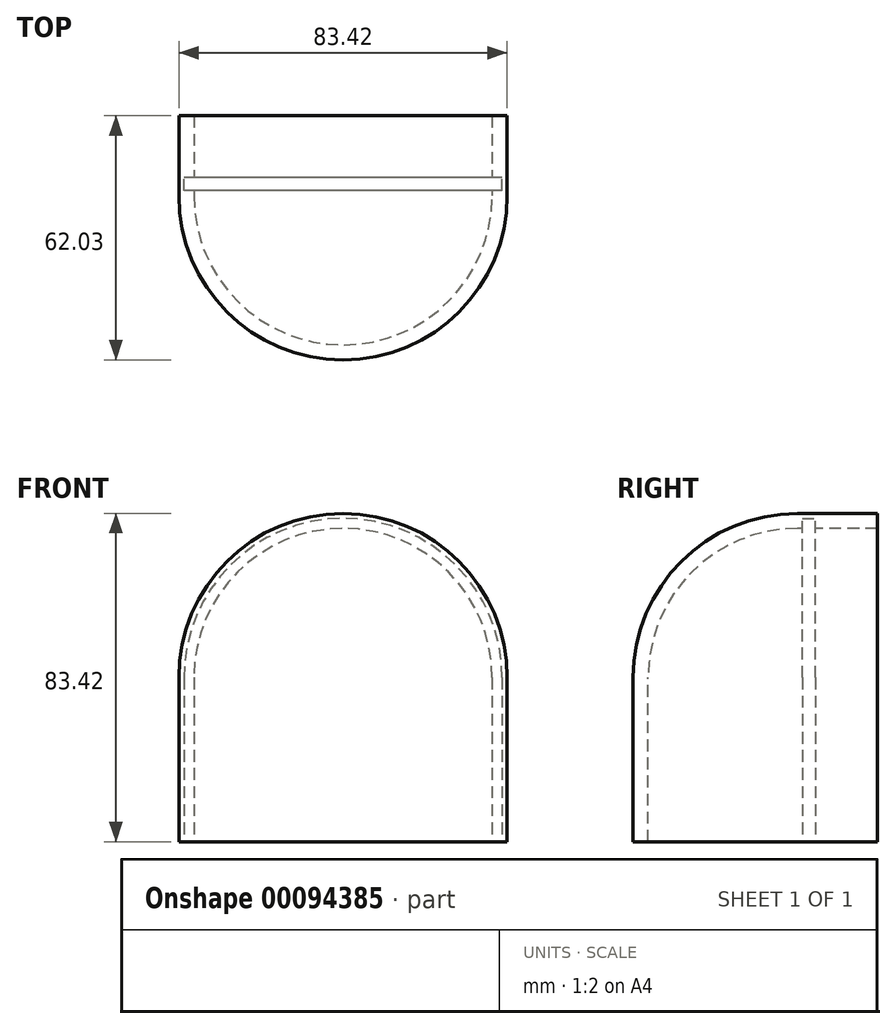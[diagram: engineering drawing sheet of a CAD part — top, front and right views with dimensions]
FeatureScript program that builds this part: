
annotation { "Feature Type Name" : "Feature", "Feature Type Description" : "" }
export const myFeature = defineFeature(function(context is Context, id is Id, definition is map)
    precondition{}
    {
        {
            var Q0;
            Q0=qCreatedBy(makeId("Front.planeOp"),FACE);
            var sketch = newSketch(context, id + "F0", { "sketchPlane" : qUnion([Q0])});
            skCircle(sketch, "E0", {"center": v(0, 0) * mm, "radius": 37.9 * mm});
            skCircle(sketch, "E1", {"center": v(0, 0) * mm, "radius": 40.44 * mm});
            skLineSegment(sketch, "E2.bottom", {"start": v(41.7, 41.7) * mm, "end": v(-41.7, 41.7) * mm});
            skLineSegment(sketch, "E2.top", {"start": v(41.7, -41.7) * mm, "end": v(-41.7, -41.7) * mm});
            skLineSegment(sketch, "E2.left", {"start": v(41.7, 41.7) * mm, "end": v(41.7, -41.7) * mm});
            skLineSegment(sketch, "E2.right", {"start": v(-41.7, 41.7) * mm, "end": v(-41.7, -41.7) * mm});
            skLineSegment(sketch, "E3", {"start": v(-37.9, 0) * mm, "end": v(-37.9, -41.7) * mm});
            skLineSegment(sketch, "E4", {"start": v(37.9, 0) * mm, "end": v(37.9, -41.7) * mm});
            skCircle(sketch, "E5", {"center": v(0, 0) * mm, "radius": 41.7 * mm});
            skLineSegment(sketch, "E6", {"start": v(-37.9, 0) * mm, "end": v(-41.7, 0) * mm});
            skLineSegment(sketch, "E7", {"start": v(37.9, 0) * mm, "end": v(41.7, 0) * mm});
            skLineSegment(sketch, "E8", {"start": v(-40.44, 0) * mm, "end": v(-40.44, -41.7) * mm});
            skLineSegment(sketch, "E9", {"start": v(40.44, 0) * mm, "end": v(40.44, -41.7) * mm});
            skSolve(sketch);
        }
        {
            var Q0;
            {var subQ0=sQuery(id+"F0.wireOp",EDGE,"E6");var subQ1=sQuery(id+"F0.wireOp",EDGE,"E0");var subQ2=makeQuery(id+"F0.imprint","INTERSECT",VERTEX,{"derivedFrom":[subQ1,sQuery(id+"F0.wireOp",EDGE,"E3"),subQ0]});Q0=makeQuery(id+"F0.imprint","IMPRINT",FACE,{"disambiguationData":[TD([[makeQuery(id+"F0.imprint","IMPRINT",EDGE,{"disambiguationData":[TD([[subQ2,1.0]])],"derivedFrom":subQ1}),-1.0]])]});}
            var Q1;
            {var subQ1=sQuery(id+"F0.wireOp",EDGE,"E5");var subQ3=makeQuery(id+"F0.imprint","INTERSECT",VERTEX,{"derivedFrom":[sQuery(id+"F0.wireOp",EDGE,"E2.bottom"),subQ1]});Q1=makeQuery(id+"F0.imprint","IMPRINT",FACE,{"disambiguationData":[TD([[makeQuery(id+"F0.imprint","IMPRINT",EDGE,{"disambiguationData":[TD([[subQ3,1.0]])],"derivedFrom":subQ1}),1.0]])]});}
            var Q2;
            {var subQ1=sQuery(id+"F0.wireOp",EDGE,"E1");var subQ3=sQuery(id+"F0.wireOp",EDGE,"E3");var subQ4=makeQuery(id+"F0.imprint","INTERSECT",VERTEX,{"derivedFrom":[subQ1,subQ3]});Q2=makeQuery(id+"F0.imprint","IMPRINT",FACE,{"disambiguationData":[TD([[makeQuery(id+"F0.imprint","IMPRINT",EDGE,{"disambiguationData":[TD([[subQ4,1.0]])],"derivedFrom":subQ1}),1.0]])]});}
            var Q3;
            {var subQ1=sQuery(id+"F0.wireOp",EDGE,"E5");var subQ3=sQuery(id+"F0.wireOp",EDGE,"E8");var subQ4=makeQuery(id+"F0.imprint","INTERSECT",VERTEX,{"derivedFrom":[subQ1,subQ3]});Q3=makeQuery(id+"F0.imprint","IMPRINT",FACE,{"disambiguationData":[TD([[makeQuery(id+"F0.imprint","IMPRINT",EDGE,{"disambiguationData":[TD([[subQ4,1.0]])],"derivedFrom":subQ1}),1.0]])]});}
            var Q4;
            {var subQ1=sQuery(id+"F0.wireOp",EDGE,"E1");var subQ3=sQuery(id+"F0.wireOp",EDGE,"E3");var subQ4=makeQuery(id+"F0.imprint","INTERSECT",VERTEX,{"derivedFrom":[subQ1,subQ3]});Q4=makeQuery(id+"F0.imprint","IMPRINT",FACE,{"disambiguationData":[TD([[makeQuery(id+"F0.imprint","IMPRINT",EDGE,{"disambiguationData":[TD([[subQ4,-1.0]])],"derivedFrom":subQ3}),-1.0]])]});}
            var Q5;
            {var subQ0=sQuery(id+"F0.wireOp",EDGE,"E3");var subQ1=sQuery(id+"F0.wireOp",EDGE,"E2.top");var subQ2=makeQuery(id+"F0.imprint","INTERSECT",VERTEX,{"derivedFrom":[subQ1,subQ0]});Q5=makeQuery(id+"F0.imprint","IMPRINT",FACE,{"disambiguationData":[TD([[makeQuery(id+"F0.imprint","IMPRINT",EDGE,{"disambiguationData":[TD([[subQ2,-1.0]])],"derivedFrom":subQ1}),-1.0]])]});}
            var Q6;
            {var subQ0=sQuery(id+"F0.wireOp",EDGE,"E2.right");var subQ1=sQuery(id+"F0.wireOp",EDGE,"E2.top");var subQ2=makeQuery(id+"F0.imprint","INTERSECT",VERTEX,{"derivedFrom":[subQ1,subQ0]});Q6=makeQuery(id+"F0.imprint","IMPRINT",FACE,{"disambiguationData":[TD([[makeQuery(id+"F0.imprint","IMPRINT",EDGE,{"disambiguationData":[TD([[subQ2,1.0]])],"derivedFrom":subQ1}),-1.0]])]});}
            var Q7;
            {var subQ1=sQuery(id+"F0.wireOp",EDGE,"E5");var subQ3=sQuery(id+"F0.wireOp",EDGE,"E9");var subQ4=makeQuery(id+"F0.imprint","INTERSECT",VERTEX,{"derivedFrom":[subQ1,subQ3]});Q7=makeQuery(id+"F0.imprint","IMPRINT",FACE,{"disambiguationData":[TD([[makeQuery(id+"F0.imprint","IMPRINT",EDGE,{"disambiguationData":[TD([[subQ4,-1.0]])],"derivedFrom":subQ1}),1.0]])]});}
            var Q8;
            {var subQ0=sQuery(id+"F0.wireOp",EDGE,"E2.left");var subQ1=sQuery(id+"F0.wireOp",EDGE,"E2.top");var subQ2=makeQuery(id+"F0.imprint","INTERSECT",VERTEX,{"derivedFrom":[subQ1,subQ0]});Q8=makeQuery(id+"F0.imprint","IMPRINT",FACE,{"disambiguationData":[TD([[makeQuery(id+"F0.imprint","IMPRINT",EDGE,{"disambiguationData":[TD([[subQ2,-1.0]])],"derivedFrom":subQ1}),-1.0]])]});}
            var Q9;
            {var subQ0=sQuery(id+"F0.wireOp",EDGE,"E4");var subQ1=sQuery(id+"F0.wireOp",EDGE,"E2.top");var subQ2=makeQuery(id+"F0.imprint","INTERSECT",VERTEX,{"derivedFrom":[subQ1,subQ0]});Q9=makeQuery(id+"F0.imprint","IMPRINT",FACE,{"disambiguationData":[TD([[makeQuery(id+"F0.imprint","IMPRINT",EDGE,{"disambiguationData":[TD([[subQ2,1.0]])],"derivedFrom":subQ1}),-1.0]])]});}
            var Q10;
            {var subQ1=sQuery(id+"F0.wireOp",EDGE,"E1");var subQ3=sQuery(id+"F0.wireOp",EDGE,"E4");var subQ4=makeQuery(id+"F0.imprint","INTERSECT",VERTEX,{"derivedFrom":[subQ1,subQ3]});Q10=makeQuery(id+"F0.imprint","IMPRINT",FACE,{"disambiguationData":[TD([[makeQuery(id+"F0.imprint","IMPRINT",EDGE,{"disambiguationData":[TD([[subQ4,-1.0]])],"derivedFrom":subQ3}),1.0]])]});}
            var Q11;
            {var subQ1=sQuery(id+"F0.wireOp",EDGE,"E1");var subQ3=sQuery(id+"F0.wireOp",EDGE,"E4");var subQ4=makeQuery(id+"F0.imprint","INTERSECT",VERTEX,{"derivedFrom":[subQ1,subQ3]});Q11=makeQuery(id+"F0.imprint","IMPRINT",FACE,{"disambiguationData":[TD([[makeQuery(id+"F0.imprint","IMPRINT",EDGE,{"disambiguationData":[TD([[subQ4,-1.0]])],"derivedFrom":subQ1}),1.0]])]});}
            extrude(context, id + "F1", {"entities" : qUnion([Q0, Q1, Q2, Q3, Q4, Q5, Q6, Q7, Q8, Q9, Q10, Q11]), "oppositeDirection" : true, "depth" : 15.75 * mm});
        }
        {
            var Q0;
            {var subQ1=sQuery(id+"F0.wireOp",EDGE,"E5");var subQ3=makeQuery(id+"F0.imprint","INTERSECT",VERTEX,{"derivedFrom":[sQuery(id+"F0.wireOp",EDGE,"E2.bottom"),subQ1]});Q0=makeQuery(id+"F0.imprint","IMPRINT",FACE,{"disambiguationData":[TD([[makeQuery(id+"F0.imprint","IMPRINT",EDGE,{"disambiguationData":[TD([[subQ3,1.0]])],"derivedFrom":subQ1}),1.0]])]});}
            var Q1;
            {var subQ0=sQuery(id+"F0.wireOp",EDGE,"E6");var subQ1=sQuery(id+"F0.wireOp",EDGE,"E0");var subQ2=makeQuery(id+"F0.imprint","INTERSECT",VERTEX,{"derivedFrom":[subQ1,sQuery(id+"F0.wireOp",EDGE,"E3"),subQ0]});Q1=makeQuery(id+"F0.imprint","IMPRINT",FACE,{"disambiguationData":[TD([[makeQuery(id+"F0.imprint","IMPRINT",EDGE,{"disambiguationData":[TD([[subQ2,1.0]])],"derivedFrom":subQ1}),-1.0]])]});}
            var Q2;
            {var subQ1=sQuery(id+"F0.wireOp",EDGE,"E1");var subQ3=sQuery(id+"F0.wireOp",EDGE,"E3");var subQ4=makeQuery(id+"F0.imprint","INTERSECT",VERTEX,{"derivedFrom":[subQ1,subQ3]});Q2=makeQuery(id+"F0.imprint","IMPRINT",FACE,{"disambiguationData":[TD([[makeQuery(id+"F0.imprint","IMPRINT",EDGE,{"disambiguationData":[TD([[subQ4,1.0]])],"derivedFrom":subQ1}),1.0]])]});}
            var Q3;
            {var subQ1=sQuery(id+"F0.wireOp",EDGE,"E1");var subQ3=sQuery(id+"F0.wireOp",EDGE,"E3");var subQ4=makeQuery(id+"F0.imprint","INTERSECT",VERTEX,{"derivedFrom":[subQ1,subQ3]});Q3=makeQuery(id+"F0.imprint","IMPRINT",FACE,{"disambiguationData":[TD([[makeQuery(id+"F0.imprint","IMPRINT",EDGE,{"disambiguationData":[TD([[subQ4,-1.0]])],"derivedFrom":subQ3}),-1.0]])]});}
            var Q4;
            {var subQ1=sQuery(id+"F0.wireOp",EDGE,"E5");var subQ3=sQuery(id+"F0.wireOp",EDGE,"E8");var subQ4=makeQuery(id+"F0.imprint","INTERSECT",VERTEX,{"derivedFrom":[subQ1,subQ3]});Q4=makeQuery(id+"F0.imprint","IMPRINT",FACE,{"disambiguationData":[TD([[makeQuery(id+"F0.imprint","IMPRINT",EDGE,{"disambiguationData":[TD([[subQ4,1.0]])],"derivedFrom":subQ1}),1.0]])]});}
            var Q5;
            {var subQ0=sQuery(id+"F0.wireOp",EDGE,"E2.right");var subQ1=sQuery(id+"F0.wireOp",EDGE,"E2.top");var subQ2=makeQuery(id+"F0.imprint","INTERSECT",VERTEX,{"derivedFrom":[subQ1,subQ0]});Q5=makeQuery(id+"F0.imprint","IMPRINT",FACE,{"disambiguationData":[TD([[makeQuery(id+"F0.imprint","IMPRINT",EDGE,{"disambiguationData":[TD([[subQ2,1.0]])],"derivedFrom":subQ1}),-1.0]])]});}
            var Q6;
            {var subQ0=sQuery(id+"F0.wireOp",EDGE,"E3");var subQ1=sQuery(id+"F0.wireOp",EDGE,"E2.top");var subQ2=makeQuery(id+"F0.imprint","INTERSECT",VERTEX,{"derivedFrom":[subQ1,subQ0]});Q6=makeQuery(id+"F0.imprint","IMPRINT",FACE,{"disambiguationData":[TD([[makeQuery(id+"F0.imprint","IMPRINT",EDGE,{"disambiguationData":[TD([[subQ2,-1.0]])],"derivedFrom":subQ1}),-1.0]])]});}
            var Q7;
            {var subQ1=sQuery(id+"F0.wireOp",EDGE,"E1");var subQ3=sQuery(id+"F0.wireOp",EDGE,"E4");var subQ4=makeQuery(id+"F0.imprint","INTERSECT",VERTEX,{"derivedFrom":[subQ1,subQ3]});Q7=makeQuery(id+"F0.imprint","IMPRINT",FACE,{"disambiguationData":[TD([[makeQuery(id+"F0.imprint","IMPRINT",EDGE,{"disambiguationData":[TD([[subQ4,-1.0]])],"derivedFrom":subQ1}),1.0]])]});}
            var Q8;
            {var subQ1=sQuery(id+"F0.wireOp",EDGE,"E5");var subQ3=sQuery(id+"F0.wireOp",EDGE,"E9");var subQ4=makeQuery(id+"F0.imprint","INTERSECT",VERTEX,{"derivedFrom":[subQ1,subQ3]});Q8=makeQuery(id+"F0.imprint","IMPRINT",FACE,{"disambiguationData":[TD([[makeQuery(id+"F0.imprint","IMPRINT",EDGE,{"disambiguationData":[TD([[subQ4,-1.0]])],"derivedFrom":subQ1}),1.0]])]});}
            var Q9;
            {var subQ0=sQuery(id+"F0.wireOp",EDGE,"E2.left");var subQ1=sQuery(id+"F0.wireOp",EDGE,"E2.top");var subQ2=makeQuery(id+"F0.imprint","INTERSECT",VERTEX,{"derivedFrom":[subQ1,subQ0]});Q9=makeQuery(id+"F0.imprint","IMPRINT",FACE,{"disambiguationData":[TD([[makeQuery(id+"F0.imprint","IMPRINT",EDGE,{"disambiguationData":[TD([[subQ2,-1.0]])],"derivedFrom":subQ1}),-1.0]])]});}
            var Q10;
            {var subQ1=sQuery(id+"F0.wireOp",EDGE,"E1");var subQ3=sQuery(id+"F0.wireOp",EDGE,"E4");var subQ4=makeQuery(id+"F0.imprint","INTERSECT",VERTEX,{"derivedFrom":[subQ1,subQ3]});Q10=makeQuery(id+"F0.imprint","IMPRINT",FACE,{"disambiguationData":[TD([[makeQuery(id+"F0.imprint","IMPRINT",EDGE,{"disambiguationData":[TD([[subQ4,-1.0]])],"derivedFrom":subQ3}),1.0]])]});}
            var Q11;
            {var subQ0=sQuery(id+"F0.wireOp",EDGE,"E4");var subQ1=sQuery(id+"F0.wireOp",EDGE,"E2.top");var subQ2=makeQuery(id+"F0.imprint","INTERSECT",VERTEX,{"derivedFrom":[subQ1,subQ0]});Q11=makeQuery(id+"F0.imprint","IMPRINT",FACE,{"disambiguationData":[TD([[makeQuery(id+"F0.imprint","IMPRINT",EDGE,{"disambiguationData":[TD([[subQ2,1.0]])],"derivedFrom":subQ1}),-1.0]])]});}
            extrude(context, id + "F2", {"entities" : qUnion([Q0, Q1, Q2, Q3, Q4, Q5, Q6, Q7, Q8, Q9, Q10, Q11]), "operationType" : NewBodyOperationType.ADD, "depth" : 4.57 * mm});
        }
        {
            var Q0;
            {var subQ0=sQuery(id+"F0.wireOp",EDGE,"E6");var subQ1=sQuery(id+"F0.wireOp",EDGE,"E0");var subQ2=makeQuery(id+"F0.imprint","INTERSECT",VERTEX,{"derivedFrom":[subQ1,sQuery(id+"F0.wireOp",EDGE,"E3"),subQ0]});Q0=makeQuery(id+"F0.imprint","IMPRINT",FACE,{"disambiguationData":[TD([[makeQuery(id+"F0.imprint","IMPRINT",EDGE,{"disambiguationData":[TD([[subQ2,1.0]])],"derivedFrom":subQ1}),-1.0]])]});}
            var Q1;
            {var subQ1=sQuery(id+"F0.wireOp",EDGE,"E1");var subQ3=sQuery(id+"F0.wireOp",EDGE,"E3");var subQ4=makeQuery(id+"F0.imprint","INTERSECT",VERTEX,{"derivedFrom":[subQ1,subQ3]});Q1=makeQuery(id+"F0.imprint","IMPRINT",FACE,{"disambiguationData":[TD([[makeQuery(id+"F0.imprint","IMPRINT",EDGE,{"disambiguationData":[TD([[subQ4,1.0]])],"derivedFrom":subQ1}),1.0]])]});}
            var Q2;
            {var subQ1=sQuery(id+"F0.wireOp",EDGE,"E1");var subQ3=sQuery(id+"F0.wireOp",EDGE,"E3");var subQ4=makeQuery(id+"F0.imprint","INTERSECT",VERTEX,{"derivedFrom":[subQ1,subQ3]});Q2=makeQuery(id+"F0.imprint","IMPRINT",FACE,{"disambiguationData":[TD([[makeQuery(id+"F0.imprint","IMPRINT",EDGE,{"disambiguationData":[TD([[subQ4,-1.0]])],"derivedFrom":subQ3}),-1.0]])]});}
            var Q3;
            {var subQ0=sQuery(id+"F0.wireOp",EDGE,"E3");var subQ1=sQuery(id+"F0.wireOp",EDGE,"E2.top");var subQ2=makeQuery(id+"F0.imprint","INTERSECT",VERTEX,{"derivedFrom":[subQ1,subQ0]});Q3=makeQuery(id+"F0.imprint","IMPRINT",FACE,{"disambiguationData":[TD([[makeQuery(id+"F0.imprint","IMPRINT",EDGE,{"disambiguationData":[TD([[subQ2,-1.0]])],"derivedFrom":subQ1}),-1.0]])]});}
            var Q4;
            {var subQ1=sQuery(id+"F0.wireOp",EDGE,"E1");var subQ3=sQuery(id+"F0.wireOp",EDGE,"E4");var subQ4=makeQuery(id+"F0.imprint","INTERSECT",VERTEX,{"derivedFrom":[subQ1,subQ3]});Q4=makeQuery(id+"F0.imprint","IMPRINT",FACE,{"disambiguationData":[TD([[makeQuery(id+"F0.imprint","IMPRINT",EDGE,{"disambiguationData":[TD([[subQ4,-1.0]])],"derivedFrom":subQ1}),1.0]])]});}
            var Q5;
            {var subQ1=sQuery(id+"F0.wireOp",EDGE,"E1");var subQ3=sQuery(id+"F0.wireOp",EDGE,"E4");var subQ4=makeQuery(id+"F0.imprint","INTERSECT",VERTEX,{"derivedFrom":[subQ1,subQ3]});Q5=makeQuery(id+"F0.imprint","IMPRINT",FACE,{"disambiguationData":[TD([[makeQuery(id+"F0.imprint","IMPRINT",EDGE,{"disambiguationData":[TD([[subQ4,-1.0]])],"derivedFrom":subQ3}),1.0]])]});}
            var Q6;
            {var subQ0=sQuery(id+"F0.wireOp",EDGE,"E4");var subQ1=sQuery(id+"F0.wireOp",EDGE,"E2.top");var subQ2=makeQuery(id+"F0.imprint","INTERSECT",VERTEX,{"derivedFrom":[subQ1,subQ0]});Q6=makeQuery(id+"F0.imprint","IMPRINT",FACE,{"disambiguationData":[TD([[makeQuery(id+"F0.imprint","IMPRINT",EDGE,{"disambiguationData":[TD([[subQ2,1.0]])],"derivedFrom":subQ1}),-1.0]])]});}
            extrude(context, id + "F3", {"entities" : qUnion([Q0, Q1, Q2, Q3, Q4, Q5, Q6]), "operationType" : NewBodyOperationType.REMOVE, "depth" : 3.3 * mm});
        }
        {
            var Q0;
            Q0=makeQuery(id+"F2.opExtrude","CAP_FACE",FACE,{"disambiguationData":[OSD([sQuery(id+"F0.wireOp",EDGE,"E0"),sQuery(id+"F0.wireOp",EDGE,"E2.top"),sQuery(id+"F0.wireOp",EDGE,"E2.left"),sQuery(id+"F0.wireOp",EDGE,"E2.right"),sQuery(id+"F0.wireOp",EDGE,"E3"),sQuery(id+"F0.wireOp",EDGE,"E4"),sQuery(id+"F0.wireOp",EDGE,"E5")])],"isStart":false});
            var sketch = newSketch(context, id + "F4", { "sketchPlane" : qUnion([Q0])});
            skLineSegment(sketch, "E10", {"start": v(-37.9, 0) * mm, "end": v(-41.7, 0) * mm});
            skLineSegment(sketch, "E11", {"start": v(37.9, 0) * mm, "end": v(41.7, 0) * mm});
            skSolve(sketch);
        }
        {
            var Q0;
            Q0=makeQuery(id+"F4.imprint","IMPRINT",FACE,{"disambiguationData":[TD([[makeQuery(id+"F4.imprint","IMPRINT",EDGE,{"derivedFrom":sQuery(id+"F4.wireOp",EDGE,"E10")}),-1.0]])]});
            var Q1;
            Q1=sQuery(id+"F4.wireOp",EDGE,"E11");
            revolve(context, id + "F5", {"operationType" : NewBodyOperationType.ADD, "entities" : qUnion([Q0]), "axis" : qUnion([Q1]), "revolveType" : RevolveType.ONE_DIRECTION, "angle" : 90 * degree});
        }
        {
            var Q0;
            Q0=makeQuery(id+"F5.opRevolve","CAP_FACE",FACE,{"disambiguationData":[OSD([sQuery(id+"F0.wireOp",EDGE,"E0"),sQuery(id+"F0.wireOp",EDGE,"E5"),sQuery(id+"F4.wireOp",EDGE,"E10"),sQuery(id+"F4.wireOp",EDGE,"E11")])],"isStart":false});
            extrude(context, id + "F6", {"entities" : qUnion([Q0]), "operationType" : NewBodyOperationType.ADD, "depth" : 41.7 * mm});
        }
    });
